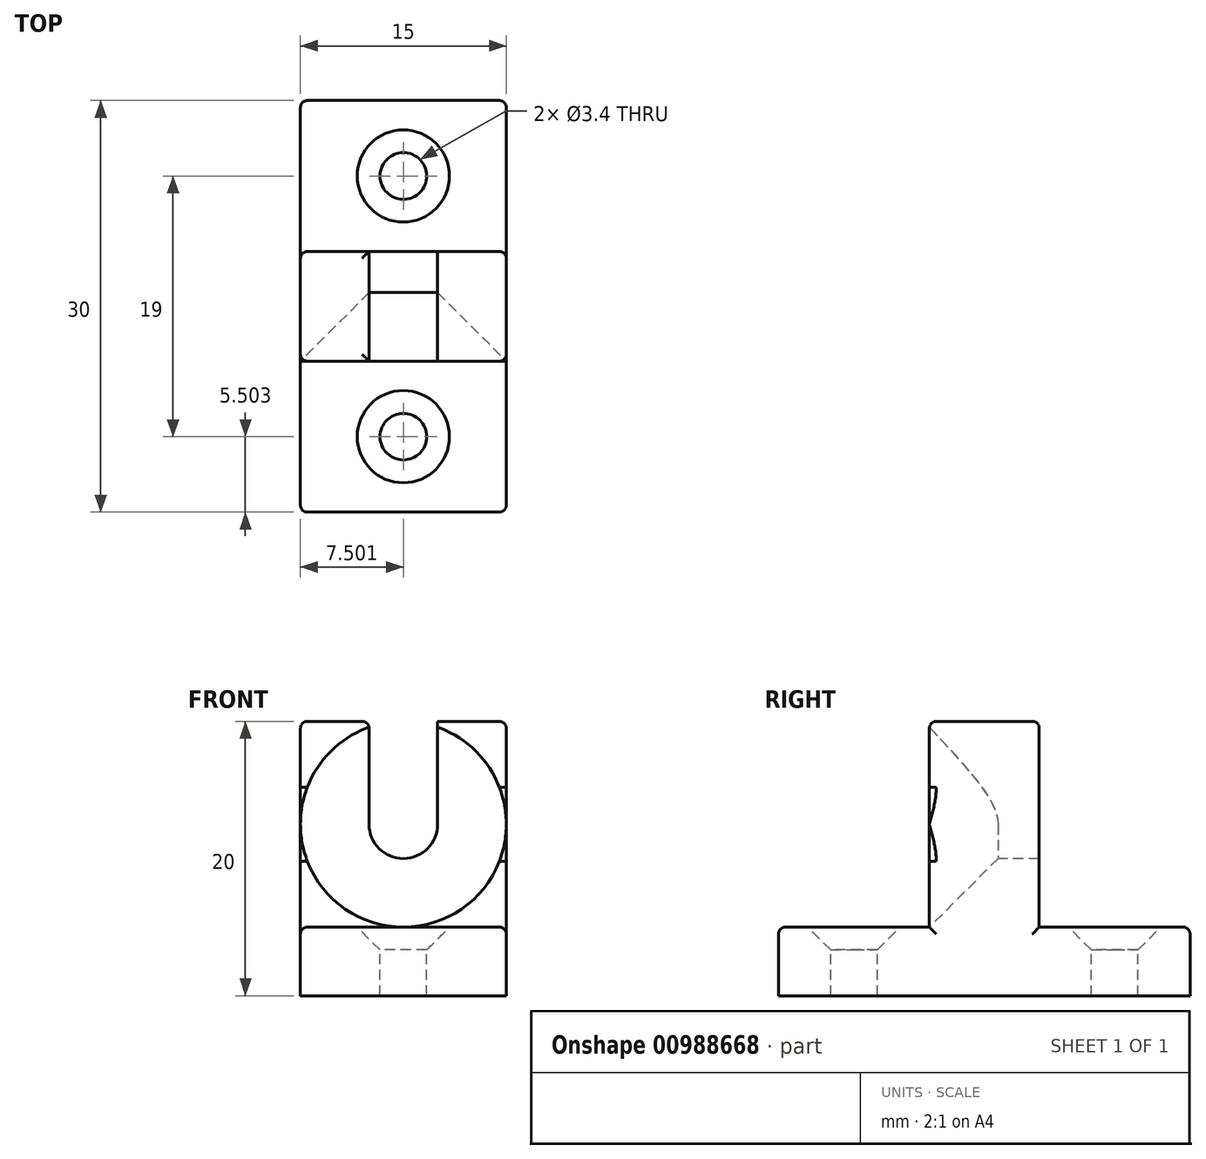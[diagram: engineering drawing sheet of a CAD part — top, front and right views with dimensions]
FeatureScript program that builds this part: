
annotation { "Feature Type Name" : "Feature", "Feature Type Description" : "" }
export const myFeature = defineFeature(function(context is Context, id is Id, definition is map)
    precondition{}
    {
        {
            var Q0;
            Q0=qCreatedBy(makeId("Top.planeOp"),FACE);
            var sketch = newSketch(context, id + "F0", { "sketchPlane" : qUnion([Q0])});
            skLineSegment(sketch, "E0.bottom", {"start": v(-10.55, 16.81) * mm, "end": v(4.45, 16.81) * mm});
            skLineSegment(sketch, "E0.top", {"start": v(-10.55, -13.19) * mm, "end": v(4.45, -13.19) * mm});
            skLineSegment(sketch, "E0.left", {"start": v(-10.55, 16.81) * mm, "end": v(-10.55, -13.19) * mm});
            skLineSegment(sketch, "E0.right", {"start": v(4.45, 16.81) * mm, "end": v(4.45, -13.19) * mm});
            skLineSegment(sketch, "E1", {"start": v(-10.55, 5.81) * mm, "end": v(4.45, 5.81) * mm});
            skLineSegment(sketch, "E2", {"start": v(-10.55, -2.19) * mm, "end": v(4.45, -2.19) * mm});
            skLineSegment(sketch, "E3", {"start": v(4.45, 5.81) * mm, "end": v(4.45, -2.19) * mm});
            skLineSegment(sketch, "E4", {"start": v(-10.55, -2.19) * mm, "end": v(-10.55, 5.81) * mm});
            skLineSegment(sketch, "E5", {"start": v(-10.55, -2.19) * mm, "end": v(-10.55, -13.19) * mm});
            skLineSegment(sketch, "E6", {"start": v(-10.55, 16.81) * mm, "end": v(-10.55, 5.81) * mm});
            skSolve(sketch);
        }
        {
            var Q0;
            {var subQ2=sQuery(id+"F0.wireOp",EDGE,"E1");Q0=makeQuery(id+"F0.imprint","IMPRINT",FACE,{"disambiguationData":[TD([[makeQuery(id+"F0.imprint","IMPRINT",EDGE,{"derivedFrom":subQ2}),-1.0]])]});}
            extrude(context, id + "F1", {"entities" : qUnion([Q0]), "depth" : 20 * mm, "offsetDistance" : 25 * mm});
        }
        {
            var Q0;
            {var subQ0=sQuery(id+"F0.wireOp",EDGE,"E0.top");Q0=makeQuery(id+"F0.imprint","IMPRINT",FACE,{"disambiguationData":[TD([[makeQuery(id+"F0.imprint","IMPRINT",EDGE,{"derivedFrom":subQ0}),1.0]])]});}
            var Q1;
            {var subQ0=sQuery(id+"F0.wireOp",EDGE,"E0.bottom");Q1=makeQuery(id+"F0.imprint","IMPRINT",FACE,{"disambiguationData":[TD([[makeQuery(id+"F0.imprint","IMPRINT",EDGE,{"derivedFrom":subQ0}),-1.0]])]});}
            extrude(context, id + "F2", {"entities" : qUnion([Q0, Q1]), "operationType" : NewBodyOperationType.ADD, "depth" : 5 * mm, "offsetDistance" : 25 * mm});
        }
        {
            var Q0;
            Q0=makeQuery(id+"F1.opExtrude","SWEPT_FACE",FACE,{"disambiguationData":[OSD([sQuery(id+"F0.wireOp",EDGE,"E2")])]});
            var sketch = newSketch(context, id + "F3", { "sketchPlane" : qUnion([Q0])});
            skLineSegment(sketch, "E7", {"start": v(4.45, 5) * mm, "end": v(-10.55, 20) * mm});
            skLineSegment(sketch, "E8", {"start": v(-10.55, 5) * mm, "end": v(4.45, 20) * mm});
            skPoint(sketch, "E9", {"position": v(-3.05, 12.5) * mm});
            skSolve(sketch);
        }
        {
            var Q0;
            Q0=sQuery(id+"F3.wireOp",VERTEX,"E9");
            var Q1;
            Q1=makeQuery(id+"F1.opExtrude","SWEPT_BODY",BODY,{"disambiguationData":[OSD([sQuery(id+"F0.wireOp",EDGE,"E0.left"),sQuery(id+"F0.wireOp",EDGE,"E0.right"),sQuery(id+"F0.wireOp",EDGE,"E1"),sQuery(id+"F0.wireOp",EDGE,"E2")])]});
            hole(context, id + "F4", {"style" : HoleStyle.C_SINK, "endStyle" : HoleEndStyle.BLIND, "holeDiameter" : 5 * mm, "cSinkDiameter" : 15 * mm, "cSinkAngle" : 90 * degree, "majorDiameter" : 5 * mm, "holeDepth" : 25 * mm, "isTappedThrough" : true, "tappedDepth" : 27.6 * mm, "tapClearance" : 3, "startFromSketch" : true, "locations" : qUnion([Q0]), "scope" : qUnion([Q1])});
        }
        {
            var Q0;
            Q0=makeQuery(id+"F1.opExtrude","CAP_FACE",FACE,{"disambiguationData":[OSD([sQuery(id+"F0.wireOp",EDGE,"E0.left"),sQuery(id+"F0.wireOp",EDGE,"E0.right"),sQuery(id+"F0.wireOp",EDGE,"E1"),sQuery(id+"F0.wireOp",EDGE,"E2")])],"isStart":false});
            var sketch = newSketch(context, id + "F5", { "sketchPlane" : qUnion([Q0])});
            skLineSegment(sketch, "E10", {"start": v(-10.55, 5.81) * mm, "end": v(4.45, -2.19) * mm, "construction": true});
            skLineSegment(sketch, "E11", {"start": v(-10.55, -2.19) * mm, "end": v(4.45, 5.81) * mm, "construction": true});
            skLineSegment(sketch, "E12.bottom", {"start": v(-0.55, -2.19) * mm, "end": v(-5.55, -2.19) * mm});
            skLineSegment(sketch, "E12.top", {"start": v(-0.55, 5.81) * mm, "end": v(-5.55, 5.81) * mm});
            skLineSegment(sketch, "E12.left", {"start": v(-0.55, -2.19) * mm, "end": v(-0.55, 5.81) * mm});
            skLineSegment(sketch, "E12.right", {"start": v(-5.55, -2.19) * mm, "end": v(-5.55, 5.81) * mm});
            skPoint(sketch, "E12.middle", {"position": v(-3.05, 1.81) * mm});
            skSolve(sketch);
        }
        {
            var Q0;
            Q0 = qSketchRegion(id + "F5", true);
            extrude(context, id + "F6", {"entities" : qUnion([Q0]), "operationType" : NewBodyOperationType.REMOVE, "endBound" : BoundingType.UP_TO_NEXT, "oppositeDirection" : true, "depth" : 25 * mm, "offsetDistance" : 25 * mm});
        }
        {
            var Q0;
            Q0=makeQuery(id+"F2.opExtrude","CAP_FACE",FACE,{"disambiguationData":[OSD([sQuery(id+"F0.wireOp",EDGE,"E0.bottom"),sQuery(id+"F0.wireOp",EDGE,"E0.left"),sQuery(id+"F0.wireOp",EDGE,"E0.right"),sQuery(id+"F0.wireOp",EDGE,"E1")])],"isStart":false});
            var sketch = newSketch(context, id + "F7", { "sketchPlane" : qUnion([Q0])});
            skLineSegment(sketch, "E13", {"start": v(4.45, -2.19) * mm, "end": v(-10.55, -13.19) * mm, "construction": true});
            skLineSegment(sketch, "E14", {"start": v(4.45, -13.19) * mm, "end": v(-10.55, -2.19) * mm, "construction": true});
            skLineSegment(sketch, "E15", {"start": v(-10.55, 16.81) * mm, "end": v(4.45, 5.81) * mm, "construction": true});
            skLineSegment(sketch, "E16", {"start": v(-10.55, 5.81) * mm, "end": v(4.45, 16.81) * mm, "construction": true});
            skPoint(sketch, "E17", {"position": v(-3.05, 11.31) * mm});
            skPoint(sketch, "E18", {"position": v(-3.05, -7.69) * mm});
            skSolve(sketch);
        }
        {
            var Q0;
            Q0=sQuery(id+"F7.wireOp",VERTEX,"E17");
            var Q1;
            Q1=sQuery(id+"F7.wireOp",VERTEX,"E18");
            var Q2;
            Q2=makeQuery(id+"F1.opExtrude","SWEPT_BODY",BODY,{"disambiguationData":[OSD([sQuery(id+"F0.wireOp",EDGE,"E0.left"),sQuery(id+"F0.wireOp",EDGE,"E0.right"),sQuery(id+"F0.wireOp",EDGE,"E1"),sQuery(id+"F0.wireOp",EDGE,"E2")])]});
            hole(context, id + "F8", {"style" : HoleStyle.C_SINK, "endStyle" : HoleEndStyle.BLIND, "standardTappedOrClearance" : lookupTablePath({ "fit" : "Normal", "standard" : "ISO", "size" : "M3", "type" : "Clearance" }), "standardBlindInLast" : lookupTablePath({ "fit" : "Normal", "standard" : "ISO", "engagement" : "75%", "pitch" : "0.5 mm", "size" : "M3", "type" : "Clearance & tapped" }), "holeDiameter" : 3.4 * mm, "cSinkDiameter" : 6.72 * mm, "cSinkAngle" : 90 * degree, "majorDiameter" : 5 * mm, "holeDepth" : 25 * mm, "isTappedThrough" : true, "tappedDepth" : 27.6 * mm, "tapClearance" : 3, "startFromSketch" : true, "locations" : qUnion([Q0, Q1]), "scope" : qUnion([Q2])});
        }
        {
            var Q0;
            {var subQ0=sQuery(id+"F0.wireOp",EDGE,"E0.left");Q0=makeQuery(id+"F2.opExtrude","CAP_EDGE",EDGE,{"disambiguationData":[OSD([subQ0]),TDD([makeQuery(id+"F0.imprint","IMPRINT",EDGE,{"disambiguationData":[TD([[makeQuery(id+"F0.imprint","INTERSECT",VERTEX,{"derivedFrom":[sQuery(id+"F0.wireOp",EDGE,"E0.bottom"),subQ0]}),-1.0]])],"derivedFrom":subQ0})])],"isStart":false});}
            var Q1;
            Q1=makeQuery(id+"F1.opExtrude","SWEPT_EDGE",EDGE,{"disambiguationData":[OSD([sQuery(id+"F0.wireOp",EDGE,"E0.left"),sQuery(id+"F0.wireOp",EDGE,"E1")])]});
            var Q2;
            Q2=makeQuery(id+"F1.opExtrude","CAP_EDGE",EDGE,{"disambiguationData":[OSD([sQuery(id+"F0.wireOp",EDGE,"E0.left")])],"isStart":false});
            var Q3;
            {var subQ0=sQuery(id+"F0.wireOp",EDGE,"E0.left");var subQ1=sQuery(id+"F0.wireOp",EDGE,"E2");var subQ2=sQuery(id+"F0.wireOp",EDGE,"E1");Q3=makeQuery(id+"F4.hole-0.boolean.opBoolean","SPLIT",EDGE,{"disambiguationData":[TD([makeQuery(id+"F1.opExtrude","CAP_FACE",FACE,{"disambiguationData":[OSD([subQ0,sQuery(id+"F0.wireOp",EDGE,"E0.right"),subQ2,subQ1])],"isStart":false})])],"derivedFrom":makeQuery(id+"F1.opExtrude","SWEPT_EDGE",EDGE,{"disambiguationData":[OSD([subQ0,subQ1])]})});}
            var Q4;
            {var subQ0=sQuery(id+"F0.wireOp",EDGE,"E0.left");var subQ1=sQuery(id+"F0.wireOp",EDGE,"E0.top");var subQ2=sQuery(id+"F0.wireOp",EDGE,"E2");Q4=makeQuery(id+"F4.hole-0.boolean.opBoolean","SPLIT",EDGE,{"disambiguationData":[TD([makeQuery(id+"F2.opExtrude","CAP_FACE",FACE,{"disambiguationData":[OSD([subQ1,subQ0,sQuery(id+"F0.wireOp",EDGE,"E0.right"),subQ2])],"isStart":false})])],"derivedFrom":makeQuery(id+"F1.opExtrude","SWEPT_EDGE",EDGE,{"disambiguationData":[OSD([subQ0,subQ2])]})});}
            var Q5;
            {var subQ0=sQuery(id+"F0.wireOp",EDGE,"E0.left");Q5=makeQuery(id+"F2.opExtrude","CAP_EDGE",EDGE,{"disambiguationData":[OSD([subQ0]),TDD([makeQuery(id+"F0.imprint","IMPRINT",EDGE,{"disambiguationData":[TD([[makeQuery(id+"F0.imprint","INTERSECT",VERTEX,{"derivedFrom":[sQuery(id+"F0.wireOp",EDGE,"E0.top"),subQ0]}),1.0]])],"derivedFrom":subQ0})])],"isStart":false});}
            var Q6;
            Q6=makeQuery(id+"F2.opExtrude","CAP_EDGE",EDGE,{"disambiguationData":[OSD([sQuery(id+"F0.wireOp",EDGE,"E0.top")])],"isStart":false});
            var Q7;
            {var subQ0=sQuery(id+"F0.wireOp",EDGE,"E0.right");Q7=makeQuery(id+"F2.opExtrude","CAP_EDGE",EDGE,{"disambiguationData":[OSD([subQ0]),TDD([makeQuery(id+"F0.imprint","IMPRINT",EDGE,{"disambiguationData":[TD([[makeQuery(id+"F0.imprint","INTERSECT",VERTEX,{"derivedFrom":[sQuery(id+"F0.wireOp",EDGE,"E0.top"),subQ0]}),1.0]])],"derivedFrom":subQ0})])],"isStart":false});}
            var Q8;
            {var subQ0=sQuery(id+"F0.wireOp",EDGE,"E0.right");var subQ1=sQuery(id+"F0.wireOp",EDGE,"E0.top");var subQ2=sQuery(id+"F0.wireOp",EDGE,"E2");Q8=makeQuery(id+"F4.hole-0.boolean.opBoolean","SPLIT",EDGE,{"disambiguationData":[TD([makeQuery(id+"F2.opExtrude","CAP_FACE",FACE,{"disambiguationData":[OSD([subQ1,sQuery(id+"F0.wireOp",EDGE,"E0.left"),subQ0,subQ2])],"isStart":false})])],"derivedFrom":makeQuery(id+"F1.opExtrude","SWEPT_EDGE",EDGE,{"disambiguationData":[OSD([subQ0,subQ2])]})});}
            var Q9;
            {var subQ0=sQuery(id+"F0.wireOp",EDGE,"E0.right");var subQ1=sQuery(id+"F0.wireOp",EDGE,"E2");var subQ2=sQuery(id+"F0.wireOp",EDGE,"E1");Q9=makeQuery(id+"F4.hole-0.boolean.opBoolean","SPLIT",EDGE,{"disambiguationData":[TD([makeQuery(id+"F1.opExtrude","CAP_FACE",FACE,{"disambiguationData":[OSD([sQuery(id+"F0.wireOp",EDGE,"E0.left"),subQ0,subQ2,subQ1])],"isStart":false})])],"derivedFrom":makeQuery(id+"F1.opExtrude","SWEPT_EDGE",EDGE,{"disambiguationData":[OSD([subQ0,subQ1])]})});}
            var Q10;
            Q10=makeQuery(id+"F1.opExtrude","CAP_EDGE",EDGE,{"disambiguationData":[OSD([sQuery(id+"F0.wireOp",EDGE,"E0.right")])],"isStart":false});
            var Q11;
            Q11=makeQuery(id+"F1.opExtrude","SWEPT_EDGE",EDGE,{"disambiguationData":[OSD([sQuery(id+"F0.wireOp",EDGE,"E0.right"),sQuery(id+"F0.wireOp",EDGE,"E1")])]});
            var Q12;
            {var subQ0=sQuery(id+"F0.wireOp",EDGE,"E0.right");Q12=makeQuery(id+"F2.opExtrude","CAP_EDGE",EDGE,{"disambiguationData":[OSD([subQ0]),TDD([makeQuery(id+"F0.imprint","IMPRINT",EDGE,{"disambiguationData":[TD([[makeQuery(id+"F0.imprint","INTERSECT",VERTEX,{"derivedFrom":[sQuery(id+"F0.wireOp",EDGE,"E0.bottom"),subQ0]}),-1.0]])],"derivedFrom":subQ0})])],"isStart":false});}
            var Q13;
            Q13=makeQuery(id+"F2.opExtrude","CAP_EDGE",EDGE,{"disambiguationData":[OSD([sQuery(id+"F0.wireOp",EDGE,"E0.bottom")])],"isStart":false});
            var Q14;
            Q14=makeQuery(id+"F2.opExtrude","SWEPT_EDGE",EDGE,{"disambiguationData":[OSD([sQuery(id+"F0.wireOp",EDGE,"E0.top"),sQuery(id+"F0.wireOp",EDGE,"E0.right")])]});
            var Q15;
            Q15=makeQuery(id+"F2.opExtrude","SWEPT_EDGE",EDGE,{"disambiguationData":[OSD([sQuery(id+"F0.wireOp",EDGE,"E0.top"),sQuery(id+"F0.wireOp",EDGE,"E0.left")])]});
            var Q16;
            Q16=makeQuery(id+"F2.opExtrude","SWEPT_EDGE",EDGE,{"disambiguationData":[OSD([sQuery(id+"F0.wireOp",EDGE,"E0.bottom"),sQuery(id+"F0.wireOp",EDGE,"E0.left")])]});
            var Q17;
            Q17=makeQuery(id+"F2.opExtrude","SWEPT_EDGE",EDGE,{"disambiguationData":[OSD([sQuery(id+"F0.wireOp",EDGE,"E0.bottom"),sQuery(id+"F0.wireOp",EDGE,"E0.right")])]});
            var Q18;
            Q18=makeQuery(id+"F6.boolean.opBoolean","COPY",EDGE,{"derivedFrom":makeQuery(id+"F6.opExtrude","CAP_EDGE",EDGE,{"disambiguationData":[OSD([sQuery(id+"F5.wireOp",EDGE,"E12.left")])],"isStart":true})});
            var Q19;
            Q19=makeQuery(id+"F6.boolean.opBoolean","COPY",EDGE,{"derivedFrom":makeQuery(id+"F6.opExtrude","CAP_EDGE",EDGE,{"disambiguationData":[OSD([sQuery(id+"F5.wireOp",EDGE,"E12.right")])],"isStart":true})});
            var Q20;
            {var subQ0=sQuery(id+"F0.wireOp",EDGE,"E0.right");var subQ2=sQuery(id+"F0.wireOp",EDGE,"E1");Q20=makeQuery(id+"F6.boolean.opBoolean","SPLIT",EDGE,{"disambiguationData":[TD([makeQuery(id+"F1.opExtrude","SWEPT_FACE",FACE,{"disambiguationData":[OSD([subQ0])]})])],"derivedFrom":makeQuery(id+"F1.opExtrude","CAP_EDGE",EDGE,{"disambiguationData":[OSD([subQ2])],"isStart":false})});}
            var Q21;
            {var subQ0=sQuery(id+"F0.wireOp",EDGE,"E1");var subQ1=sQuery(id+"F0.wireOp",EDGE,"E0.left");Q21=makeQuery(id+"F6.boolean.opBoolean","SPLIT",EDGE,{"disambiguationData":[TD([makeQuery(id+"F1.opExtrude","SWEPT_FACE",FACE,{"disambiguationData":[OSD([subQ1])]})])],"derivedFrom":makeQuery(id+"F1.opExtrude","CAP_EDGE",EDGE,{"disambiguationData":[OSD([subQ0])],"isStart":false})});}
            var Q22;
            {var subQ0=sQuery(id+"F0.wireOp",EDGE,"E0.right");var subQ1=sQuery(id+"F0.wireOp",EDGE,"E2");Q22=makeQuery(id+"F4.hole-0.boolean.opBoolean","SPLIT",EDGE,{"disambiguationData":[TD([makeQuery(id+"F1.opExtrude","SWEPT_FACE",FACE,{"disambiguationData":[OSD([subQ0])]})])],"derivedFrom":makeQuery(id+"F1.opExtrude","CAP_EDGE",EDGE,{"disambiguationData":[OSD([subQ1])],"isStart":false})});}
            var Q23;
            {var subQ0=sQuery(id+"F0.wireOp",EDGE,"E0.left");var subQ1=sQuery(id+"F0.wireOp",EDGE,"E2");Q23=makeQuery(id+"F4.hole-0.boolean.opBoolean","SPLIT",EDGE,{"disambiguationData":[TD([makeQuery(id+"F1.opExtrude","SWEPT_FACE",FACE,{"disambiguationData":[OSD([subQ0])]})])],"derivedFrom":makeQuery(id+"F1.opExtrude","CAP_EDGE",EDGE,{"disambiguationData":[OSD([subQ1])],"isStart":false})});}
            var Q24;
            Q24=makeQuery(id+"F6.boolean.opBoolean","COPY",EDGE,{"derivedFrom":makeQuery(id+"F6.opExtrude","CAP_EDGE",EDGE,{"disambiguationData":[OSD([sQuery(id+"F5.wireOp",EDGE,"E12.left")]),topologyDisambiguationEdgeConnected([makeQuery(id+"F4.hole-0.boolean.opBoolean","COPY",FACE,{"derivedFrom":makeQuery(id+"F4.hole-0.opRevolve","SWEPT_FACE",FACE,{"disambiguationData":[OSD([sQuery(id+"F4.hole-0.sketch.wireOp",EDGE,"csink_start_line_1")])]})})])],"isStart":false})});
            var Q25;
            Q25=makeQuery(id+"F4.hole-0.boolean.opBoolean","COPY",EDGE,{"derivedFrom":makeQuery(id+"F4.hole-0.opRevolve","SWEPT_EDGE",EDGE,{"disambiguationData":[OSD([sQuery(id+"F4.hole-0.sketch.wireOp",EDGE,"csink_start_line_1"),sQuery(id+"F4.hole-0.sketch.wireOp",EDGE,"core_line_2")])]})});
            var Q26;
            Q26=makeQuery(id+"F6.boolean.opBoolean","COPY",EDGE,{"derivedFrom":makeQuery(id+"F6.opExtrude","CAP_EDGE",EDGE,{"disambiguationData":[OSD([sQuery(id+"F5.wireOp",EDGE,"E12.right")]),topologyDisambiguationEdgeConnected([makeQuery(id+"F4.hole-0.boolean.opBoolean","COPY",FACE,{"derivedFrom":makeQuery(id+"F4.hole-0.opRevolve","SWEPT_FACE",FACE,{"disambiguationData":[OSD([sQuery(id+"F4.hole-0.sketch.wireOp",EDGE,"csink_start_line_1")])]})})])],"isStart":false})});
            var Q27;
            Q27=makeQuery(id+"F6.boolean.opBoolean","COPY",EDGE,{"derivedFrom":makeQuery(id+"F6.opExtrude","SWEPT_EDGE",EDGE,{"disambiguationData":[OSD([sQuery(id+"F0.wireOp",EDGE,"E1"),sQuery(id+"F5.wireOp",EDGE,"E12.top"),sQuery(id+"F5.wireOp",EDGE,"E12.left")])]})});
            var Q28;
            Q28=makeQuery(id+"F4.hole-0.boolean.opBoolean","INTERSECT",EDGE,{"derivedFrom":[makeQuery(id+"F1.opExtrude","SWEPT_FACE",FACE,{"disambiguationData":[OSD([sQuery(id+"F0.wireOp",EDGE,"E1")])]}),makeQuery(id+"F4.hole-0.opRevolve","SWEPT_FACE",FACE,{"disambiguationData":[OSD([sQuery(id+"F4.hole-0.sketch.wireOp",EDGE,"core_line_2")])]})]});
            fillet(context, id + "F9", {"entities" : qUnion([Q0, Q1, Q2, Q3, Q4, Q5, Q6, Q7, Q8, Q9, Q10, Q11, Q12, Q13, Q14, Q15, Q16, Q17, Q18, Q19, Q20, Q21, Q22, Q23, Q24, Q25, Q26, Q27, Q28]), "radius" : .5 * mm, "tangentPropagation" : true, "allowEdgeOverflow" : false});
        }
    });
